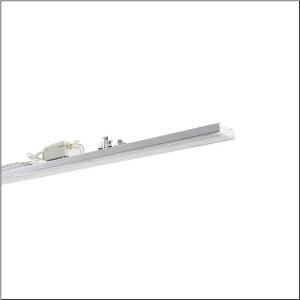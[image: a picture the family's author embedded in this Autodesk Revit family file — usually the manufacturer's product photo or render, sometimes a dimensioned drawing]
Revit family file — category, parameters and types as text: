
# Revit family: licross_r__21_recessed_mo_52te1edv4e5g_90af
name_source: partatom
category: Lighting Fixtures
units: mm (PartAtom-declared; Revit-internal decimal feet)

## family parameters
Cut with Voids When Loaded = No
Host = Face
Light Source = No
Part Type = Normal
Room Calculation Point = No
Round Connector Dimension = Use Diameter
Shared = No

## types (1)
- --- (1 x LED, 14910 lm, 85.3 W, 4000K)
    Apparent Load = 85 VA
    CIE Flux Codes = 85 95 99 100 100
    Color Rendering = 80
    Color Temperature = 4000K
    Default Elevation = 1800 mm
    Description = Licross® 21 Recessed MO, luminaire insert, of sheet steel, galvanised, coil coated, white, length: 2.250mm, width: 66mm, height: 67mm, LED rated luminous flux: 14.910lm, light colour: 840, control gear: DALI 2, with plug, 5-pole, with phase selection, mains connection: 220..240V, AC, 50/60Hz, rated input power: 85W, halogen-free wiring, primary light control with lens, of plastic, primary optical cover: cover, of PMMA, light emission: direct distribution, primary light characteristic: symmetric, protection rating (complete): IP54, insulation class (complete): insulation class I (protective earthing), certification: CE, ENEC, VDE, UKCA, protection symbol: D if used in an environment with non-conductive dust loads with corresponding accessories, impact resistance: IK06, permissible ambient temperature for indoor applications: -25..+35°C, corresponds to IFS (International Featured Standards) requirements for safety and quality in the food industry, reducing of maximum allowable ambient temperature of 5°C with ceiling mounting, LABS conformity tested according to VDMA 24364:2018-05, packaging unit: 1 piece
    Height = 58 mm
    Lamp = 1 x LED
    Lamp Light Flux = 14910 lm
    Lamp Power = 85.3 W
    Lamp count = 1
    Length = 2250 mm
    Luminous efficacy = 175 lm/W
    Manufacturer = Siteco
    ModVariant = No
    Model = 52TE1EDV4E5G
    Mounting Place = Ceiling
    Mounting Type = Pendant
    Number of Poles = 1
    OnlyDefault = Yes
    Power Factor = 1
    Product Name = Licross® 21 Recessed MO
    Product group = luminaire insert
    ProductGroupID = 901
    Protection Class = Protection class I
    Protection Degree = IP 54
    RLX_Detail_Level = 1
    RLX_Emergency_Light_Flux = 0 lm
    RLX_Emergency_Type = 0
    RLX_Emergency_Type_DB = No
    RlxData = <blob elided: 29589 chars, md5=d8871dc3>
    Socket = socket
    Standby Power = 0 W
    System Light Flux = 14910 lm
    System Power = 85 W
    Type Comments = factory setting: luminous flux: 100 % | dim-lin: 254 | 390 mA
    Type Image = l_1296930.jpg
    URL = http://relux.com
    VarID = @adj_057041
    Voltage = 0 V
    Weight = 0.00 kg
    Width = 66 mm

## geometry (parser evidence)
native form markers: Blend x4, Sweep x12
no freeform markers — native parametric forms only
